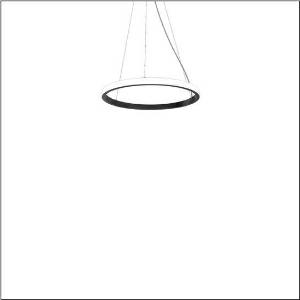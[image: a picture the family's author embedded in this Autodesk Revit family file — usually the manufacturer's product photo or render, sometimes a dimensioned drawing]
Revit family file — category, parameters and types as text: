
# Revit family: silica_r__21_ring-o_5pjbo1d1104a_1dcd
name_source: partatom
category: Lighting Fixtures
units: mm (PartAtom-declared; Revit-internal decimal feet)

## family parameters
Cut with Voids When Loaded = No
Host = Face
Light Source = No
Part Type = Normal
Room Calculation Point = No
Round Connector Dimension = Use Diameter
Shared = No

## types (1)
- Silica® 21 Ring-O (1 x LED, 3740 lm, 60 W, 3000K)
    Apparent Load = 60 VA
    CIE Flux Codes = 2 16 49 50 100
    Color Rendering = 80
    Color Temperature = 3000K
    Default Elevation = 1800 mm
    Description = Silica® 21 Ring-O, suspended luminaire, of PMMA, frosted, light emission: outer ring side luminous distribution, primary light characteristic: symmetric, installation type: suspended mounting, LED, rated luminous flux: 3.744lm, luminous efficacy: 62lm/W, light colour: 830, colour temperature: 3000K, control gear: DALI 2, with terminal, 5-pole, mains connection: 230V, AC/DC, 0/50..60Hz, rated input power: 60W, housing, of extruded aluminium section, jet black (RAL 9005), diameter: 610mm, ceiling canopy, jet black (RAL 9005), protection rating (lamp compartment): IP40, insulation class (complete): insulation class I (protective earthing), certification: CE, impact resistance: IK02, permissible operating ambient temperature: 0..+35°C, packaging unit: 1 piece
    Height = 48 mm  [stored 0.15748 ft]
    Lamp = 1 x LED
    Lamp Light Flux = 3740 lm
    Lamp Power = 60 W
    Lamp count = 1
    Length = 610 mm
    Luminous efficacy = 62 lm/W
    Manufacturer = Siteco
    ModVariant = No
    Model = 5PJBO1D1104A
    Mounting Place = Ceiling
    Mounting Type = Pendant
    Number of Poles = 1
    OnlyDefault = Yes
    Power Factor = 1
    Product Name = Silica® 21 Ring-O
    Product group = suspended luminaire
    ProductGroupID = 905
    Protection Class = Protection class I
    Protection Degree = IP 40
    RLX_Detail_Level = 1
    RLX_Emergency_Light_Flux = 0 lm
    RLX_Emergency_Type = 0
    RLX_Emergency_Type_DB = No
    RlxData = <blob elided: 12173 chars, md5=310edf7a>
    Socket = socket
    Standby Power = 0 W
    System Light Flux = 3740 lm
    System Power = 60 W
    Type Comments = Product without accessories
    Type Image = l_1258377.jpg
    URL = http://relux.com
    VarID = ---
    Voltage = 0 V
    Weight = 0.00 kg
    Width = 0 mm  [stored 0 ft]

note: [stored X ft] marks values corroborated as IEEE doubles in the binary element streams (Revit-internal decimal feet)

## geometry (parser evidence)
native form markers: Sweep x12
no freeform markers — native parametric forms only
